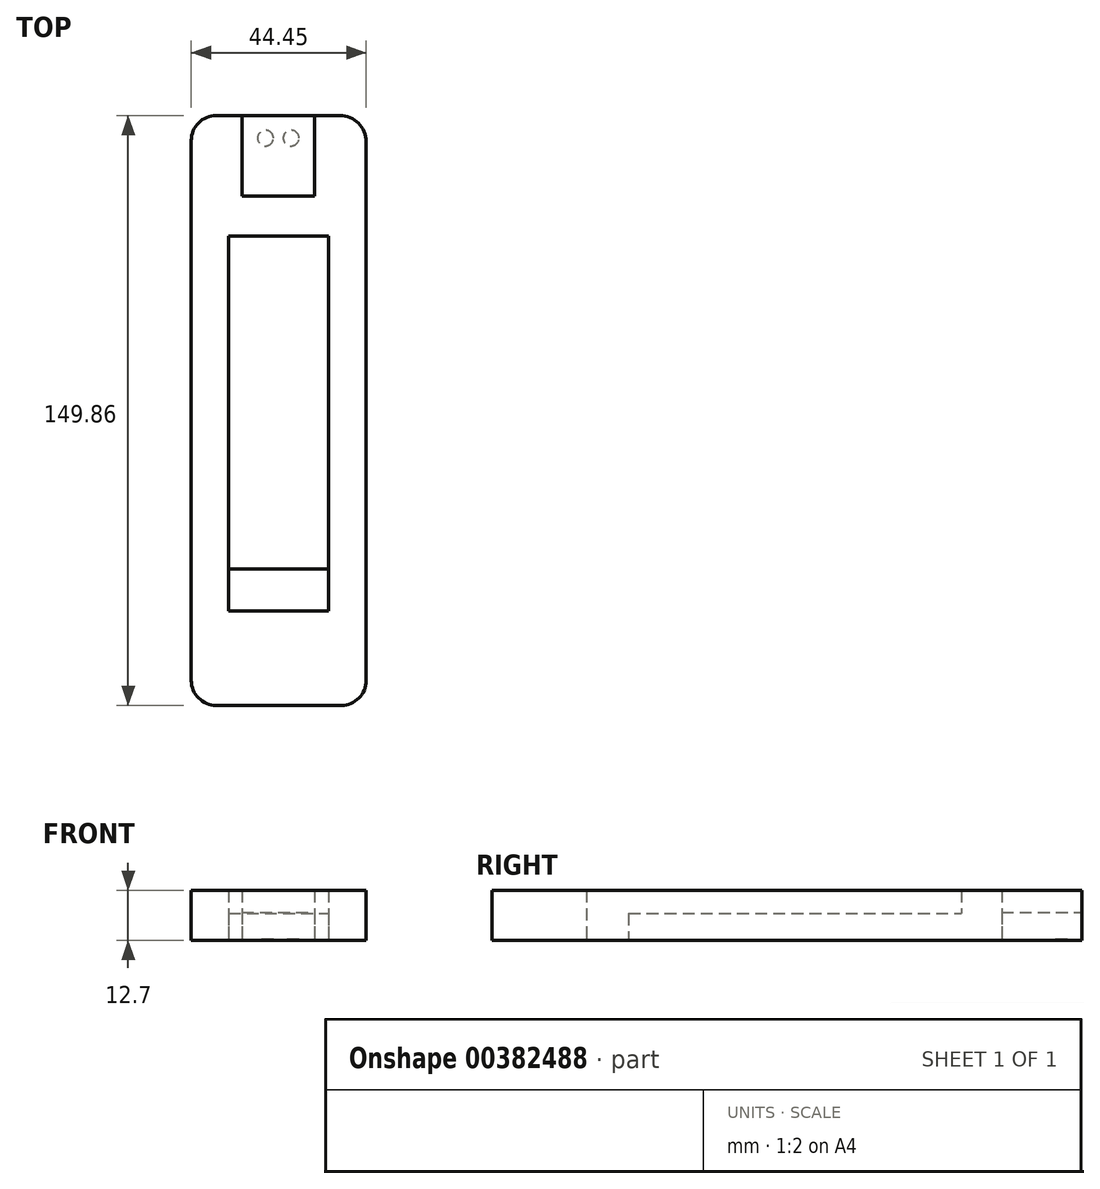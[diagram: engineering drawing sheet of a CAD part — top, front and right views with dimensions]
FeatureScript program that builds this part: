
annotation { "Feature Type Name" : "Feature", "Feature Type Description" : "" }
export const myFeature = defineFeature(function(context is Context, id is Id, definition is map)
    precondition{}
    {
        {
            var Q0;
            Q0=qCreatedBy(makeId("Top.planeOp"),FACE);
            var sketch = newSketch(context, id + "F0", { "sketchPlane" : qUnion([Q0])});
            skLineSegment(sketch, "E0.bottom", {"start": v(-23.95, 91.17) * mm, "end": v(7.45, 91.17) * mm});
            skLineSegment(sketch, "E0.top", {"start": v(-23.95, -58.7) * mm, "end": v(7.8, -58.7) * mm});
            skLineSegment(sketch, "E0.left", {"start": v(-30.3, 84.82) * mm, "end": v(-30.3, -52.34) * mm});
            skLineSegment(sketch, "E0.right", {"start": v(14.15, 84.47) * mm, "end": v(14.15, -52.34) * mm});
            skCircle(sketch, "E1", {"center": v(-11.45, 85.44) * mm, "radius": 2 * mm});
            skCircle(sketch, "E2", {"center": v(-4.95, 85.44) * mm, "radius": 2 * mm});
            skArc(sketch, "E3.filletArc", {"start": v(-23.95, 91.17) * mm, "mid": v(-28.44, 89.3) * mm, "end": v(-30.3, 84.82) * mm});
            skPoint(sketch, "E4.visualSharp", {"position": v(14.15, 91.17) * mm});
            skArc(sketch, "E4.filletArc", {"start": v(14.15, 84.47) * mm, "mid": v(12.18, 89.2) * mm, "end": v(7.45, 91.17) * mm});
            skPoint(sketch, "E5.visualSharp", {"position": v(14.15, -58.7) * mm});
            skArc(sketch, "E5.filletArc", {"start": v(7.8, -58.7) * mm, "mid": v(12.29, -56.83) * mm, "end": v(14.15, -52.34) * mm});
            skPoint(sketch, "E6.visualSharp", {"position": v(-30.3, -58.7) * mm});
            skArc(sketch, "E6.filletArc", {"start": v(-30.3, -52.34) * mm, "mid": v(-28.44, -56.83) * mm, "end": v(-23.95, -58.7) * mm});
            skLineSegment(sketch, "E7.bottom", {"start": v(-20.8, -34.76) * mm, "end": v(4.6, -34.76) * mm});
            skLineSegment(sketch, "E7.top", {"start": v(-20.8, -24.08) * mm, "end": v(4.6, -24.08) * mm});
            skLineSegment(sketch, "E7.left", {"start": v(-20.8, -34.76) * mm, "end": v(-20.8, -24.08) * mm});
            skLineSegment(sketch, "E7.right", {"start": v(4.6, -34.76) * mm, "end": v(4.6, -24.08) * mm});
            skLineSegment(sketch, "E8.left", {"start": v(-20.8, -24.08) * mm, "end": v(-20.8, -24.08) * mm});
            skLineSegment(sketch, "E8.right", {"start": v(4.6, -24.08) * mm, "end": v(4.6, -24.08) * mm});
            skLineSegment(sketch, "E9.top", {"start": v(-20.8, 60.55) * mm, "end": v(4.6, 60.55) * mm});
            skLineSegment(sketch, "E9.left", {"start": v(-20.8, -24.08) * mm, "end": v(-20.8, 60.55) * mm});
            skLineSegment(sketch, "E9.right", {"start": v(4.6, -24.08) * mm, "end": v(4.6, 60.55) * mm});
            skLineSegment(sketch, "E10.bottom", {"start": v(1.05, 70.74) * mm, "end": v(-17.45, 70.74) * mm});
            skLineSegment(sketch, "E10.top", {"start": v(1.05, 91.17) * mm, "end": v(-17.45, 91.17) * mm});
            skLineSegment(sketch, "E10.left", {"start": v(1.05, 70.74) * mm, "end": v(1.05, 91.17) * mm});
            skLineSegment(sketch, "E10.right", {"start": v(-17.45, 70.74) * mm, "end": v(-17.45, 91.17) * mm});
            skSolve(sketch);
        }
        {
            var Q0;
            Q0=makeQuery(id+"F0.imprint","IMPRINT",FACE,{"disambiguationData":[TD([[makeQuery(id+"F0.imprint","IMPRINT",EDGE,{"derivedFrom":sQuery(id+"F0.wireOp",EDGE,"E0.bottom")}),-1.0]])]});
            extrude(context, id + "F1", {"entities" : qUnion([Q0]), "depth" : 12.7 * mm, "offsetDistance" : 25.4 * mm});
        }
        {
            var Q0;
            Q0=makeQuery(id+"F0.imprint","IMPRINT",FACE,{"disambiguationData":[TD([[makeQuery(id+"F0.imprint","IMPRINT",EDGE,{"derivedFrom":sQuery(id+"F0.wireOp",EDGE,"E2")}),1.0]])]});
            var Q1;
            Q1=makeQuery(id+"F0.imprint","IMPRINT",FACE,{"disambiguationData":[TD([[makeQuery(id+"F0.imprint","IMPRINT",EDGE,{"derivedFrom":sQuery(id+"F0.wireOp",EDGE,"E1")}),1.0]])]});
            extrude(context, id + "F2", {"entities" : qUnion([Q0, Q1]), "operationType" : NewBodyOperationType.ADD, "depth" : 0.25 * mm, "offsetDistance" : 25.4 * mm});
        }
        {
            var Q0;
            Q0=makeQuery(id+"F0.imprint","IMPRINT",FACE,{"disambiguationData":[TD([[makeQuery(id+"F0.imprint","IMPRINT",EDGE,{"derivedFrom":sQuery(id+"F0.wireOp",EDGE,"E7.top")}),1.0]])]});
            extrude(context, id + "F3", {"entities" : qUnion([Q0]), "operationType" : NewBodyOperationType.ADD, "depth" : 6.86 * mm, "offsetDistance" : 25.4 * mm});
        }
        {
            var Q0;
            Q0=makeQuery(id+"F0.imprint","IMPRINT",FACE,{"disambiguationData":[TD([[makeQuery(id+"F0.imprint","IMPRINT",EDGE,{"derivedFrom":sQuery(id+"F0.wireOp",EDGE,"E1")}),1.0]])]});
            var Q1;
            Q1=makeQuery(id+"F0.imprint","IMPRINT",FACE,{"disambiguationData":[TD([[makeQuery(id+"F0.imprint","IMPRINT",EDGE,{"derivedFrom":sQuery(id+"F0.wireOp",EDGE,"E1")}),-1.0]])]});
            var Q2;
            Q2=makeQuery(id+"F0.imprint","IMPRINT",FACE,{"disambiguationData":[TD([[makeQuery(id+"F0.imprint","IMPRINT",EDGE,{"derivedFrom":sQuery(id+"F0.wireOp",EDGE,"E2")}),1.0]])]});
            extrude(context, id + "F4", {"entities" : qUnion([Q0, Q1, Q2]), "depth" : 7.11 * mm, "offsetDistance" : 25.4 * mm});
        }
    });
